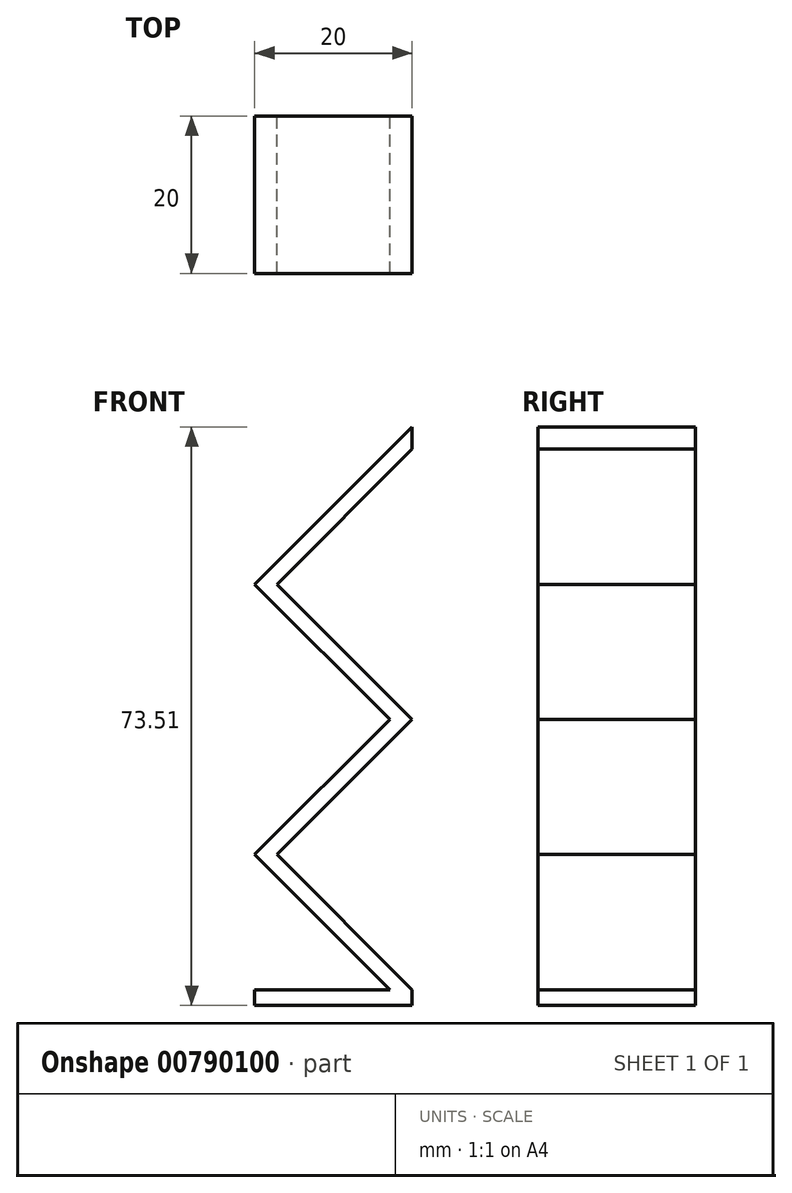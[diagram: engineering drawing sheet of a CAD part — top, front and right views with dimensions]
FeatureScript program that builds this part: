
annotation { "Feature Type Name" : "Feature", "Feature Type Description" : "" }
export const myFeature = defineFeature(function(context is Context, id is Id, definition is map)
    precondition{}
    {
        {
            var Q0;
            Q0=qCreatedBy(makeId("Front.planeOp"),FACE);
            var sketch = newSketch(context, id + "F0", { "sketchPlane" : qUnion([Q0])});
            skLineSegment(sketch, "E0.bottom", {"start": v(-10, 2) * mm, "end": v(7.17, 2) * mm});
            skLineSegment(sketch, "E0.top", {"start": v(-10, 0) * mm, "end": v(10, 0) * mm});
            skLineSegment(sketch, "E0.left", {"start": v(-10, 2) * mm, "end": v(-10, 0) * mm});
            skLineSegment(sketch, "E0.right", {"start": v(10, 2) * mm, "end": v(10, 0) * mm});
            skLineSegment(sketch, "E1", {"start": v(7.17, 2) * mm, "end": v(-10, 19.17) * mm});
            skLineSegment(sketch, "E2", {"start": v(-10, 19.17) * mm, "end": v(7.17, 36.34) * mm});
            skLineSegment(sketch, "E3", {"start": v(7.17, 36.34) * mm, "end": v(-10, 53.51) * mm});
            skPoint(sketch, "E4.orphan", {"position": v(7.17, 55.88) * mm});
            skPoint(sketch, "E5.end.orphan", {"position": v(-10, 37.92) * mm});
            skLineSegment(sketch, "E6", {"start": v(10, 2) * mm, "end": v(-7.17, 19.17) * mm});
            skLineSegment(sketch, "E7", {"start": v(-7.17, 19.17) * mm, "end": v(10, 36.34) * mm});
            skLineSegment(sketch, "E8", {"start": v(10, 36.34) * mm, "end": v(-7.17, 53.51) * mm});
            skLineSegment(sketch, "E9", {"start": v(10, 2) * mm, "end": v(10, 83.9) * mm, "construction": true});
            skLineSegment(sketch, "E10", {"start": v(-10, 0) * mm, "end": v(-10, 81) * mm, "construction": true});
            skPoint(sketch, "E11.end.orphan", {"position": v(7.17, 70.69) * mm});
            skLineSegment(sketch, "E12", {"start": v(-10, 53.51) * mm, "end": v(10, 73.51) * mm});
            skLineSegment(sketch, "E13", {"start": v(-7.17, 53.51) * mm, "end": v(10, 70.69) * mm});
            skLineSegment(sketch, "E14", {"start": v(10, 70.69) * mm, "end": v(10, 73.51) * mm});
            skSolve(sketch);
        }
        {
            var Q0;
            Q0 = qSketchRegion(id + "F0", true);
            extrude(context, id + "F1", {"entities" : qUnion([Q0]), "endBound" : BoundingType.SYMMETRIC, "depth" : 20 * mm, "offsetDistance" : 25 * mm});
        }
    });
